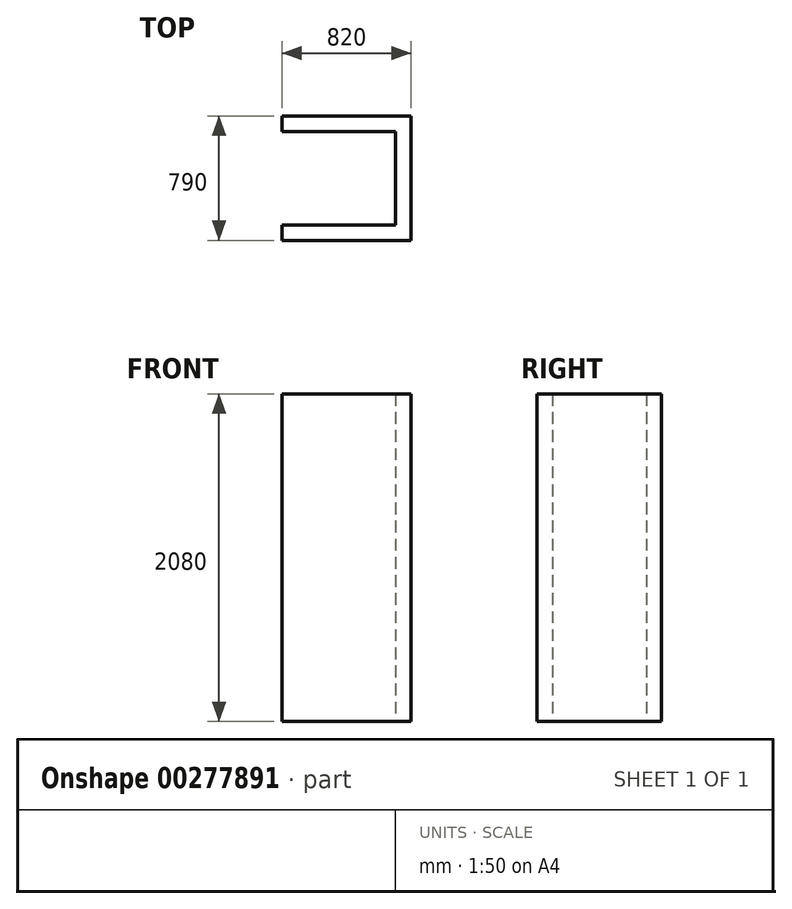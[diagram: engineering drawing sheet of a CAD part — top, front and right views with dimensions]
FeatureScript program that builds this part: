
annotation { "Feature Type Name" : "Feature", "Feature Type Description" : "" }
export const myFeature = defineFeature(function(context is Context, id is Id, definition is map)
    precondition{}
    {
        {
            var Q0;
            Q0=qCreatedBy(makeId("Top.planeOp"),FACE);
            var sketch = newSketch(context, id + "F0", { "sketchPlane" : qUnion([Q0])});
            skLineSegment(sketch, "E0", {"start": v(457.57, 110.7) * mm, "end": v(554.57, 110.7) * mm});
            skLineSegment(sketch, "E1", {"start": v(554.57, 110.7) * mm, "end": v(554.57, 930.7) * mm});
            skLineSegment(sketch, "E2", {"start": v(554.57, 930.7) * mm, "end": v(-235.43, 930.7) * mm});
            skLineSegment(sketch, "E3", {"start": v(-235.43, 930.7) * mm, "end": v(-235.43, 110.7) * mm});
            skLineSegment(sketch, "E4", {"start": v(-235.43, 110.7) * mm, "end": v(-138.43, 110.7) * mm});
            skLineSegment(sketch, "E5", {"start": v(-138.43, 110.7) * mm, "end": v(-138.43, 830.7) * mm});
            skLineSegment(sketch, "E6", {"start": v(-138.43, 830.7) * mm, "end": v(457.57, 830.7) * mm});
            skLineSegment(sketch, "E7", {"start": v(457.57, 830.7) * mm, "end": v(457.57, 110.7) * mm});
            skSolve(sketch);
        }
        {
            var Q0;
            Q0 = qSketchRegion(id + "F0", true);
            extrude(context, id + "F1", {"entities" : qUnion([Q0]), "depth" : 2080 * mm});
        }
        {
            var Q0;
            Q0=makeQuery(id+"F1.opExtrude","SWEPT_BODY",BODY,{"disambiguationData":[OSD([sQuery(id+"F0.wireOp",EDGE,"E0"),sQuery(id+"F0.wireOp",EDGE,"E1"),sQuery(id+"F0.wireOp",EDGE,"E2"),sQuery(id+"F0.wireOp",EDGE,"E3"),sQuery(id+"F0.wireOp",EDGE,"E4"),sQuery(id+"F0.wireOp",EDGE,"E5"),sQuery(id+"F0.wireOp",EDGE,"E6"),sQuery(id+"F0.wireOp",EDGE,"E7")])]});
            var Q1;
            Q1=makeQuery(id+"F1.opExtrude","SWEPT_EDGE",EDGE,{"disambiguationData":[OSD([sQuery(id+"F0.wireOp",EDGE,"E4"),sQuery(id+"F0.wireOp",EDGE,"E5")])]});
            transform(context, id + "F2", {"entities" : qUnion([Q0]), "transformType" : TransformType.ROTATION, "transformAxis" : qUnion([Q1]), "angle" : 90 * degree, "makeCopy" : false});
        }
    });
